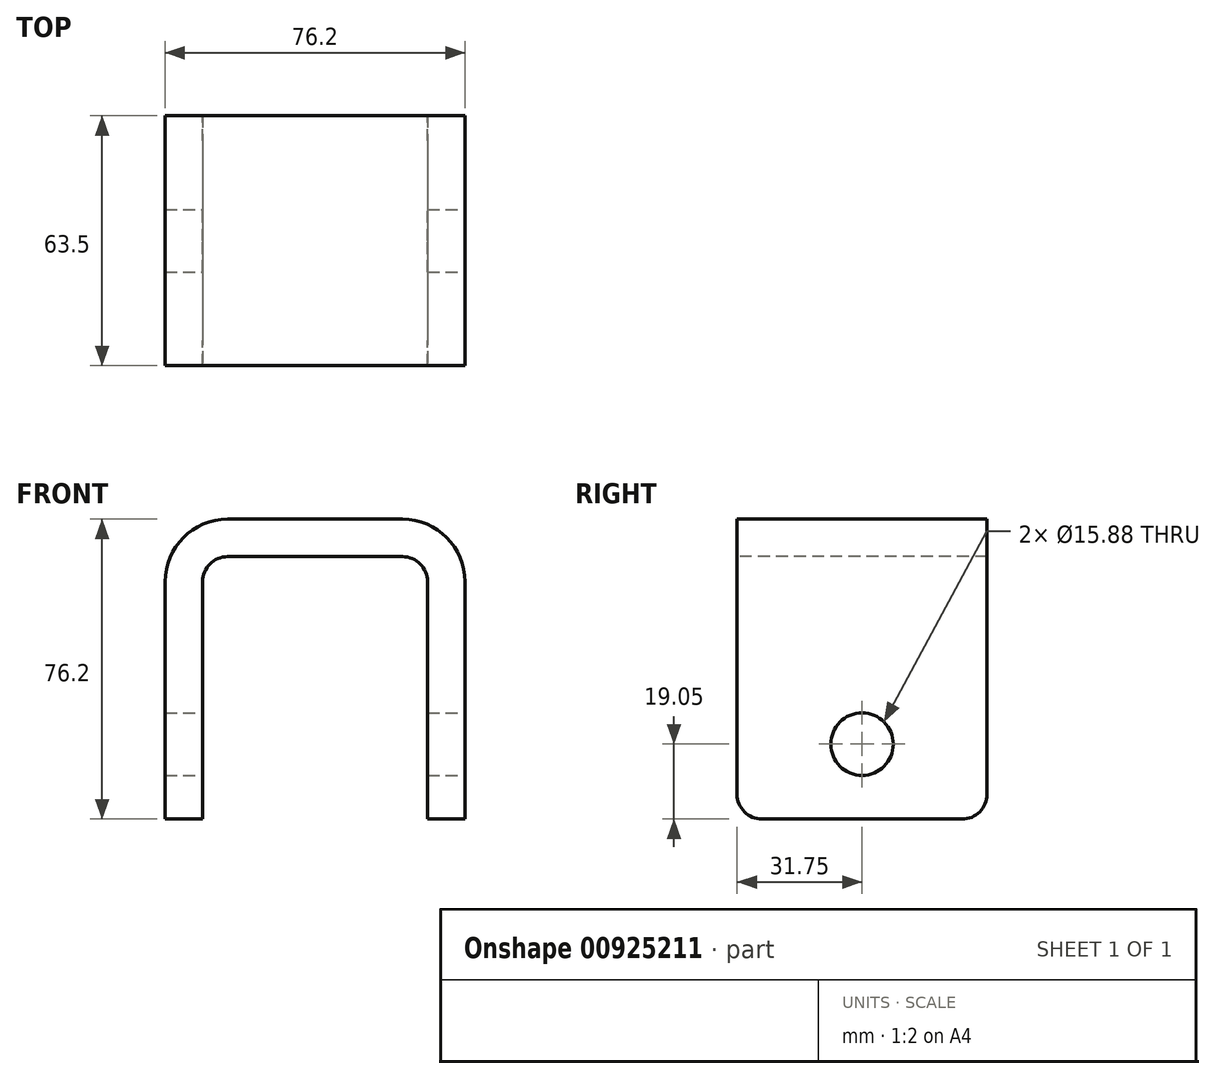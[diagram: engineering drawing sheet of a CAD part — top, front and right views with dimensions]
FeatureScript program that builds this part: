
annotation { "Feature Type Name" : "Feature", "Feature Type Description" : "" }
export const myFeature = defineFeature(function(context is Context, id is Id, definition is map)
    precondition{}
    {
        {
            var Q0;
            Q0=qCreatedBy(makeId("Front.planeOp"),FACE);
            var sketch = newSketch(context, id + "F0", { "sketchPlane" : qUnion([Q0])});
            skLineSegment(sketch, "E0.bottom", {"start": v(-30.67, 0) * mm, "end": v(45.53, 0) * mm});
            skLineSegment(sketch, "E0.top", {"start": v(-30.67, 76.2) * mm, "end": v(45.53, 76.2) * mm});
            skLineSegment(sketch, "E0.left", {"start": v(-30.67, 0) * mm, "end": v(-30.67, 76.2) * mm});
            skLineSegment(sketch, "E0.right", {"start": v(45.53, 0) * mm, "end": v(45.53, 76.2) * mm});
            skSolve(sketch);
        }
        {
            var Q0;
            Q0 = qSketchRegion(id + "F0", true);
            extrude(context, id + "F1", {"entities" : qUnion([Q0]), "oppositeDirection" : true, "depth" : 63.5 * mm, "offsetDistance" : 25.4 * mm});
        }
        {
            var Q0;
            Q0=makeQuery(id+"F1.opExtrude","CAP_FACE",FACE,{"disambiguationData":[OSD([sQuery(id+"F0.wireOp",EDGE,"E0.bottom"),sQuery(id+"F0.wireOp",EDGE,"E0.top"),sQuery(id+"F0.wireOp",EDGE,"E0.left"),sQuery(id+"F0.wireOp",EDGE,"E0.right")])],"isStart":true});
            var Q1;
            Q1=makeQuery(id+"F1.opExtrude","SWEPT_FACE",FACE,{"disambiguationData":[OSD([sQuery(id+"F0.wireOp",EDGE,"E0.bottom")])]});
            var Q2;
            Q2=makeQuery(id+"F1.opExtrude","CAP_FACE",FACE,{"disambiguationData":[OSD([sQuery(id+"F0.wireOp",EDGE,"E0.bottom"),sQuery(id+"F0.wireOp",EDGE,"E0.top"),sQuery(id+"F0.wireOp",EDGE,"E0.left"),sQuery(id+"F0.wireOp",EDGE,"E0.right")])],"isStart":false});
            shell(context, id + "F2", {"entities" : qUnion([Q0, Q1, Q2]), "thickness" : 9.52 * mm});
        }
        {
            var Q0;
            Q0=makeQuery(id+"F2.opShell","OFFSET_EDGE",EDGE,{"disambiguationData":[OSD([sQuery(id+"F0.wireOp",EDGE,"E0.top"),sQuery(id+"F0.wireOp",EDGE,"E0.left")])]});
            var Q1;
            Q1=makeQuery(id+"F2.opShell","OFFSET_EDGE",EDGE,{"disambiguationData":[OSD([sQuery(id+"F0.wireOp",EDGE,"E0.top"),sQuery(id+"F0.wireOp",EDGE,"E0.right")])]});
            fillet(context, id + "F3", {"entities" : qUnion([Q0, Q1]), "radius" : 6.35 * mm, "tangentPropagation" : true, "allowEdgeOverflow" : false});
        }
        {
            var Q0;
            Q0=makeQuery(id+"F1.opExtrude","SWEPT_EDGE",EDGE,{"disambiguationData":[OSD([sQuery(id+"F0.wireOp",EDGE,"E0.top"),sQuery(id+"F0.wireOp",EDGE,"E0.left")])]});
            var Q1;
            Q1=makeQuery(id+"F1.opExtrude","SWEPT_EDGE",EDGE,{"disambiguationData":[OSD([sQuery(id+"F0.wireOp",EDGE,"E0.top"),sQuery(id+"F0.wireOp",EDGE,"E0.right")])]});
            fillet(context, id + "F4", {"entities" : qUnion([Q0, Q1]), "radius" : 15.88 * mm, "tangentPropagation" : true, "allowEdgeOverflow" : false});
        }
        {
            var Q0;
            Q0=makeQuery(id+"F1.opExtrude","SWEPT_FACE",FACE,{"disambiguationData":[OSD([sQuery(id+"F0.wireOp",EDGE,"E0.right")])]});
            var sketch = newSketch(context, id + "F5", { "sketchPlane" : qUnion([Q0])});
            skCircle(sketch, "E1", {"center": v(31.75, 19.05) * mm, "radius": 7.94 * mm});
            skPoint(sketch, "E1.centerSnap0", {"position": v(31.75, 0) * mm});
            skSolve(sketch);
        }
        {
            var Q0;
            Q0 = qSketchRegion(id + "F5", true);
            extrude(context, id + "F6", {"entities" : qUnion([Q0]), "operationType" : NewBodyOperationType.REMOVE, "endBound" : BoundingType.THROUGH_ALL, "oppositeDirection" : true, "depth" : 25.4 * mm, "offsetDistance" : 25.4 * mm});
        }
        {
            var Q0;
            Q0=makeQuery(id+"F1.opExtrude","CAP_EDGE",EDGE,{"disambiguationData":[OSD([sQuery(id+"F0.wireOp",EDGE,"E0.bottom")])],"isStart":true});
            var Q1;
            Q1=makeQuery(id+"F1.opExtrude","CAP_EDGE",EDGE,{"disambiguationData":[OSD([sQuery(id+"F0.wireOp",EDGE,"E0.bottom")])],"isStart":false});
            var Q2;
            {var subQ0=sQuery(id+"F0.wireOp",EDGE,"E0.bottom");Q2=makeQuery(id+"F2.opShell","OFFSET_EDGE",EDGE,{"disambiguationData":[OSD([subQ0]),TDD([makeQuery(id+"F1.opExtrude","CAP_EDGE",EDGE,{"disambiguationData":[OSD([subQ0])],"isStart":true})])]});}
            var Q3;
            {var subQ0=sQuery(id+"F0.wireOp",EDGE,"E0.bottom");Q3=makeQuery(id+"F2.opShell","OFFSET_EDGE",EDGE,{"disambiguationData":[OSD([subQ0]),TDD([makeQuery(id+"F1.opExtrude","CAP_EDGE",EDGE,{"disambiguationData":[OSD([subQ0])],"isStart":false})])]});}
            fillet(context, id + "F7", {"entities" : qUnion([Q0, Q1, Q2, Q3]), "radius" : 6.35 * mm, "tangentPropagation" : true, "allowEdgeOverflow" : false});
        }
    });
